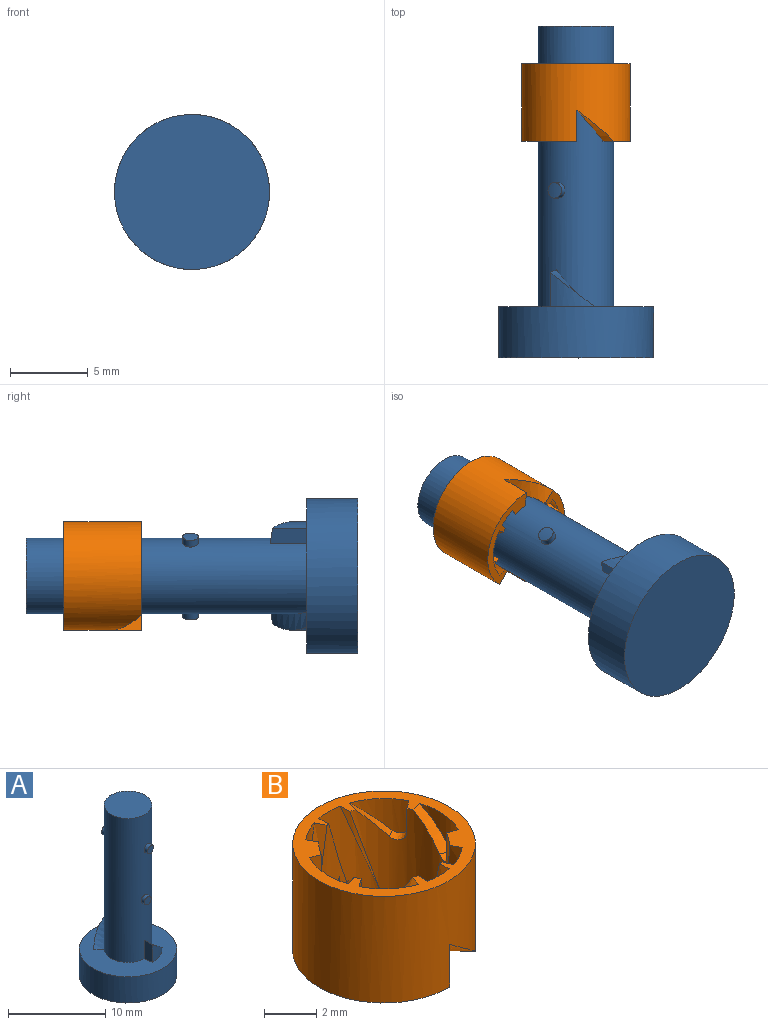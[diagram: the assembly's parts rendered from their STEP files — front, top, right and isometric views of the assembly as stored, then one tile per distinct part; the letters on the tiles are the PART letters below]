
ASSEMBLY  parts=2 mates=1
PART A: 19 faces, bbox 10.1x10.1x21.5 mm
  f0: bspline ~3.34x2.88mm, area 3.6mm2, adj f3,f7,f8,f17
  f1: plane 2.46x1.15mm, normal (-0.99,-0.16,0), area 2.4mm2, adj f2,f3,f6,f7
  f2: bspline ~3.34x2.88mm, area 3.6mm2, adj f1,f3,f6,f7
  f3: cylinder r=2.45mm len=18.1mm, axis (0,0,-1), area 270.3mm2, adj f0,f1,f2,f7,f8,f12,f13,f14
  f4: plane 10x10mm, normal (0,0,-1), area 78.5mm2, adj f5
  f5: cylinder r=5mm len=10mm, axis (0,0,1), area 103.7mm2, adj f4,f7
  f6: cylinder r=3.5mm len=2.57mm, axis (0,0,1), area 3.2mm2, adj f1,f2,f7
  f7: plane 10x10mm, normal (0,0,1), area 54.3mm2, adj f0,f1,f2,f3,f5,f6,f8,f17
  f8: plane 2.46x1.15mm, normal (0.99,0.16,0), area 2.4mm2, adj f0,f3,f7,f17
  f9: cylinder r=3mm len=1mm, axis (0,0,1), area 0.8mm2, adj f18
  f10: cylinder r=2.9mm len=1mm, axis (0,0,1), area 0.8mm2, adj f15
  f11: cylinder r=3mm len=1mm, axis (0,0,1), area 0.8mm2, adj f12
  f12: cylinder r=0.5mm len=1mm, axis (0,1,0), area 1.7mm2, adj f3,f11
  f13: plane 4.9x4.9mm, normal (0,0,1), area 18.9mm2, adj f3
  f14: cylinder r=0.5mm len=1mm, axis (0,-1,0), area 1.4mm2, adj f3,f16
  f15: cylinder r=0.5mm len=1.06mm, axis (0.16,-0.99,0), area 1.4mm2, adj f3,f10
  f16: cylinder r=2.9mm len=1mm, axis (0,0,1), area 0.8mm2, adj f14
  f17: cylinder r=3.5mm len=2.57mm, axis (0,0,1), area 3.2mm2, adj f0,f7,f8
  f18: cylinder r=0.5mm len=1.07mm, axis (-0.16,0.99,0), area 1.7mm2, adj f3,f9
PART B: 48 faces, bbox 8.1x8.1x8.1 mm
  f0: offset ~7.41x3.53mm, area 2.7mm2, adj f1,f26,f29,f45
  f1: plane 6.02x3.55mm, normal (0,0,-1), area 4.8mm2, adj f0,f5,f6,f13,f14,f22,f23,f26
  f2: offset ~7.41x3.66mm, area 2.7mm2, adj f25,f27,f29,f47
  f3: offset ~7.42x3.5mm, area 2.7mm2, adj f25,f28,f29,f46
  f4: offset ~7.41x3.53mm, area 2.7mm2, adj f25,f27,f29,f46
  f5: offset ~7.41x3.66mm, area 2.7mm2, adj f1,f26,f29,f44
  f6: offset ~7.42x3.5mm, area 2.7mm2, adj f1,f29,f31,f45
  f7: bspline ~0.83x0.72mm, area 0.5mm2, adj f18,f27,f40,f41
  f8: cylinder r=3mm len=1.71mm, axis (0,0,-1), area 2.1mm2, adj f9,f10,f29,f39
  f9: bspline ~0.88x0.86mm, area 0.5mm2, adj f8,f10,f26,f39
  f10: plane 1.17x0.41mm, normal (-0.59,0.81,0), area 0.6mm2, adj f8,f9,f26,f29
  f11: bspline ~0.83x0.72mm, area 0.5mm2, adj f12,f26,f37,f38
  f12: plane 1.17x0.49mm, normal (0.29,0.96,0), area 0.6mm2, adj f11,f26,f29,f38
  f13: cylinder r=3mm len=2.22mm, axis (0,0,1), area 2.1mm2, adj f1,f14,f32,f33
  f14: bspline ~1.91x1.79mm, area 1mm2, adj f1,f13,f26,f33
  f15: cylinder r=3mm len=2.22mm, axis (0,0,1), area 2.1mm2, adj f16,f17,f25,f34
  f16: bspline ~0.69x0.6mm, area 0.5mm2, adj f15,f17,f27,f34
  f17: bspline ~1.91x1.79mm, area 1mm2, adj f15,f16,f25,f27
  f18: cylinder r=3mm len=2.27mm, axis (0,0,-1), area 2.1mm2, adj f7,f29,f40,f41
  f19: bspline ~0.88x0.86mm, area 0.5mm2, adj f20,f27,f35,f36
  f20: cylinder r=3mm len=1.71mm, axis (0,0,-1), area 2.1mm2, adj f19,f29,f35,f36
  f21: offset ~7.42x3.72mm, area 2.7mm2, adj f25,f29,f31,f47
  f22: bspline ~3.11x2.62mm, area 3.1mm2, adj f1,f30,f31,f42
  f23: plane 2.24x1.09mm, normal (-0.99,-0.16,0), area 2.1mm2, adj f1,f24,f28,f30
  f24: bspline ~3.11x2.62mm, area 3.1mm2, adj f23,f25,f28,f30
  f25: plane 6.02x3.55mm, normal (0,0,-1), area 4.8mm2, adj f2,f3,f4,f15,f17,f21,f24,f27
  f26: cylinder r=2.5mm len=5mm, axis (0,0,1), area 13.4mm2, adj f0,f1,f5,f9,f10,f11,f12,f14
  f27: cylinder r=2.5mm len=5mm, axis (0,0,1), area 13.4mm2, adj f2,f4,f7,f16,f17,f19,f25,f29
  f28: cylinder r=2.5mm len=5mm, axis (0,0,1), area 6.2mm2, adj f1,f3,f23,f24,f25,f29,f43
  f29: plane 7x7mm, normal (0,0,1), area 12.1mm2, adj f0,f2,f3,f4,f5,f6,f8,f10
  f30: cylinder r=3.5mm len=7mm, axis (0,0,1), area 104.7mm2, adj f1,f22,f23,f24,f25,f29,f42
  f31: cylinder r=2.5mm len=5mm, axis (0,0,1), area 6.2mm2, adj f1,f6,f21,f22,f25,f29,f42
  f32: plane 1.17x0.51mm, normal (0,1,0), area 0.6mm2, adj f1,f13,f26,f33
  f33: bspline ~0.69x0.6mm, area 0.5mm2, adj f13,f14,f26,f32
  f34: plane 1.17x0.51mm, normal (0,-1,0), area 0.6mm2, adj f15,f16,f25,f27
  f35: plane 1.17x0.41mm, normal (0.59,-0.81,0), area 0.6mm2, adj f19,f20,f27,f29
  f36: bspline ~1.81x1.79mm, area 1mm2, adj f19,f20,f27,f29
  f37: bspline ~2.02x1.79mm, area 1mm2, adj f11,f26,f29,f38
  f38: cylinder r=3mm len=2.27mm, axis (0,0,-1), area 2.1mm2, adj f11,f12,f29,f37
  f39: bspline ~1.81x1.79mm, area 1mm2, adj f8,f9,f26,f29
  f40: plane 1.17x0.49mm, normal (-0.29,-0.96,0), area 0.6mm2, adj f7,f18,f27,f29
  f41: bspline ~2.02x1.79mm, area 1mm2, adj f7,f18,f27,f29
  f42: plane 2.24x1.09mm, normal (0.99,0.16,0), area 2.1mm2, adj f22,f25,f30,f31
  f43: offset ~7.42x3.72mm, area 2.7mm2, adj f1,f28,f29,f44
  f44: cylinder r=3mm len=5mm, axis (0,0,-1), area 5.9mm2, adj f1,f5,f29,f43
  f45: cylinder r=3mm len=5mm, axis (0,0,-1), area 5.9mm2, adj f0,f1,f6,f29
  f46: cylinder r=3mm len=5mm, axis (0,0,-1), area 5.9mm2, adj f3,f4,f25,f29
  f47: cylinder r=3mm len=5mm, axis (0,0,-1), area 5.9mm2, adj f2,f21,f25,f29
PLACE A rot(axis=(-0.94,-0.24,-0.24),93.5deg) t=(0,-8.37,0)mm
PLACE B rot(axis=(0,0.71,0.71),180deg) t=(0,-5.8,0)mm
MATE cylindrical B.f30 <-> A.f3  axis (0,1,0) through (0,-5,0)mm
